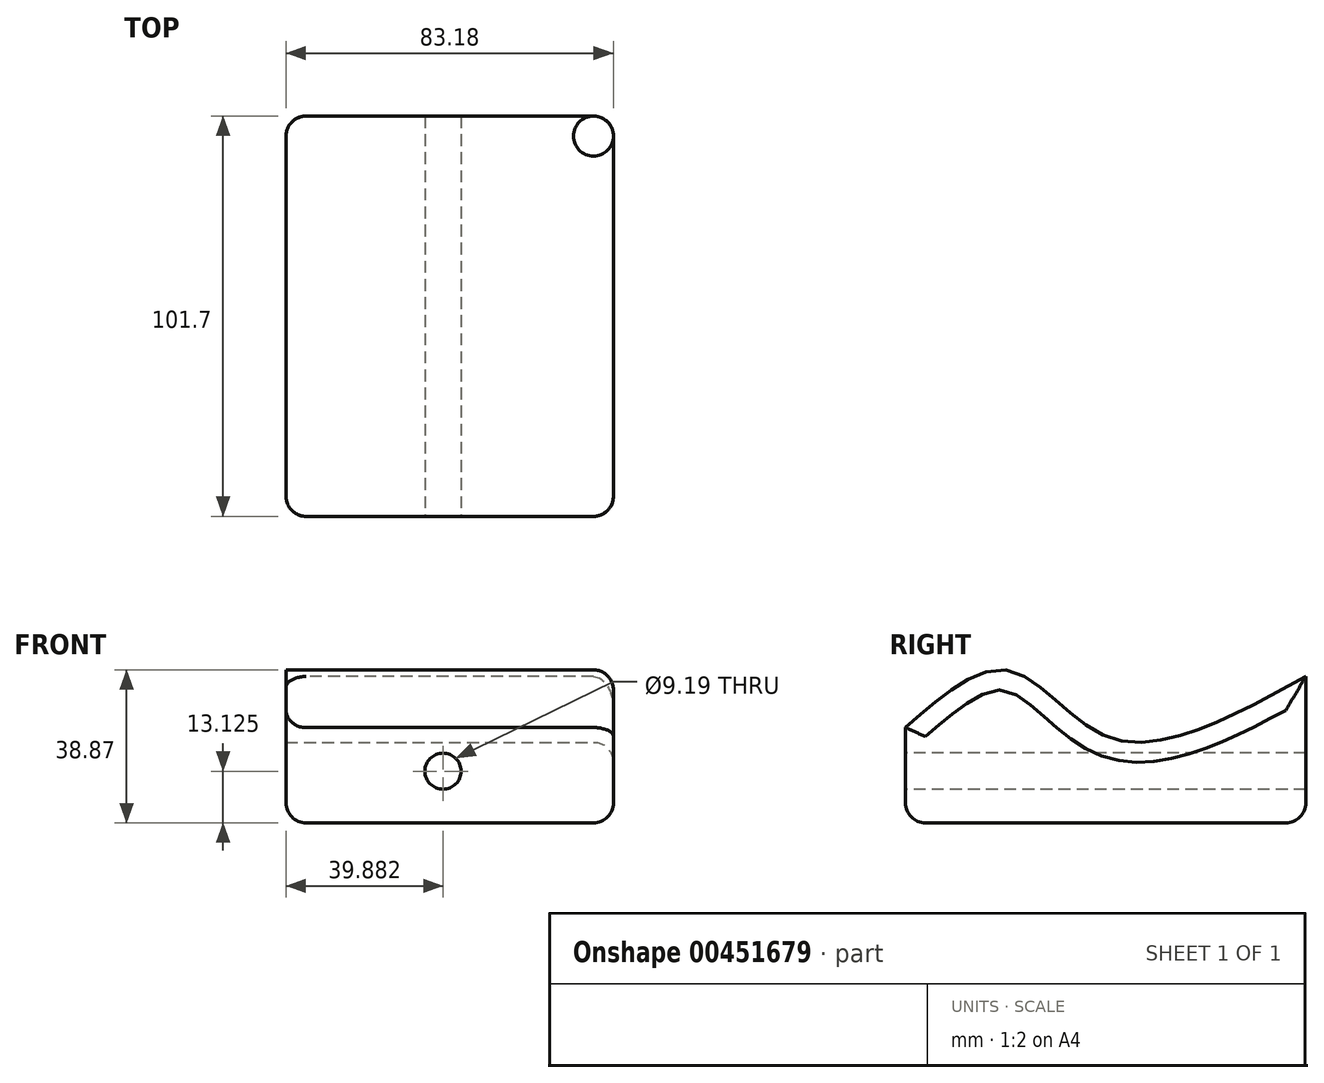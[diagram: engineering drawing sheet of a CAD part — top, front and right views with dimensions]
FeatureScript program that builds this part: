
annotation { "Feature Type Name" : "Feature", "Feature Type Description" : "" }
export const myFeature = defineFeature(function(context is Context, id is Id, definition is map)
    precondition{}
    {
        {
            var Q0;
            Q0=qCreatedBy(makeId("Top.planeOp"),FACE);
            var sketch = newSketch(context, id + "F0", { "sketchPlane" : qUnion([Q0])});
            skLineSegment(sketch, "E0.bottom", {"start": v(38.7, 44.88) * mm, "end": v(-44.47, 44.88) * mm});
            skLineSegment(sketch, "E0.top", {"start": v(38.7, -56.82) * mm, "end": v(-44.47, -56.82) * mm});
            skLineSegment(sketch, "E0.left", {"start": v(38.7, 44.88) * mm, "end": v(38.7, -56.82) * mm});
            skLineSegment(sketch, "E0.right", {"start": v(-44.47, 44.88) * mm, "end": v(-44.47, -56.82) * mm});
            skSolve(sketch);
        }
        {
            var Q0;
            Q0 = qSketchRegion(id + "F0", true);
            extrude(context, id + "F1", {"entities" : qUnion([Q0]), "depth" : 56.64 * mm});
        }
        {
            var Q0;
            Q0=makeQuery(id+"F1.opExtrude","SWEPT_FACE",FACE,{"disambiguationData":[OSD([sQuery(id+"F0.wireOp",EDGE,"E0.right")])]});
            var sketch = newSketch(context, id + "F2", { "sketchPlane" : qUnion([Q0])});
            skFitSpline(sketch, "E1", {"points": [v(-44.88, 37.17) * mm, v(4.53, 21.53) * mm, v(30.26, 38.61) * mm, v(56.82, 24.2) * mm], "startDerivative": vector(137.73, -76.07) * mm, "endDerivative": vector(91.5, -80.7) * mm});
            skLineSegment(sketch, "E2", {"start": v(-44.88, 37.17) * mm, "end": v(-44.88, 56.64) * mm});
            skLineSegment(sketch, "E3", {"start": v(-44.88, 56.64) * mm, "end": v(56.82, 56.64) * mm});
            skLineSegment(sketch, "E4", {"start": v(56.82, 56.64) * mm, "end": v(56.82, 24.2) * mm});
            skSolve(sketch);
        }
        {
            var Q0;
            Q0=makeQuery(id+"F2.imprint","IMPRINT",FACE,{"disambiguationData":[TD([[makeQuery(id+"F2.imprint","IMPRINT",EDGE,{"derivedFrom":sQuery(id+"F2.wireOp",EDGE,"E1")}),1.0]])]});
            extrude(context, id + "F3", {"entities" : qUnion([Q0]), "operationType" : NewBodyOperationType.REMOVE, "oppositeDirection" : true, "depth" : 112.01 * mm});
        }
        {
            var Q0;
            Q0=makeQuery(id+"F1.opExtrude","SWEPT_EDGE",EDGE,{"disambiguationData":[OSD([sQuery(id+"F0.wireOp",EDGE,"E0.top"),sQuery(id+"F0.wireOp",EDGE,"E0.right")])]});
            var Q1;
            Q1=makeQuery(id+"F1.opExtrude","SWEPT_EDGE",EDGE,{"disambiguationData":[OSD([sQuery(id+"F0.wireOp",EDGE,"E0.top"),sQuery(id+"F0.wireOp",EDGE,"E0.left")])]});
            var Q2;
            Q2=makeQuery(id+"F1.opExtrude","SWEPT_EDGE",EDGE,{"disambiguationData":[OSD([sQuery(id+"F0.wireOp",EDGE,"E0.bottom"),sQuery(id+"F0.wireOp",EDGE,"E0.right")])]});
            var Q3;
            Q3=makeQuery(id+"F1.opExtrude","SWEPT_EDGE",EDGE,{"disambiguationData":[OSD([sQuery(id+"F0.wireOp",EDGE,"E0.bottom"),sQuery(id+"F0.wireOp",EDGE,"E0.left")])]});
            var Q4;
            Q4=makeQuery(id+"F3.boolean.opBoolean","COPY",EDGE,{"derivedFrom":makeQuery(id+"F3.opExtrude","SWEPT_EDGE",EDGE,{"disambiguationData":[OSD([sQuery(id+"F0.wireOp",EDGE,"E0.bottom"),sQuery(id+"F0.wireOp",EDGE,"E0.right"),sQuery(id+"F2.wireOp",EDGE,"E1"),sQuery(id+"F2.wireOp",EDGE,"E2")])]})});
            var Q5;
            Q5=makeQuery(id+"F1.opExtrude","CAP_EDGE",EDGE,{"disambiguationData":[OSD([sQuery(id+"F0.wireOp",EDGE,"E0.bottom")])],"isStart":true});
            var Q6;
            Q6=makeQuery(id+"F3.boolean.opBoolean","INTERSECT",EDGE,{"derivedFrom":[makeQuery(id+"F1.opExtrude","SWEPT_FACE",FACE,{"disambiguationData":[OSD([sQuery(id+"F0.wireOp",EDGE,"E0.left")])]}),makeQuery(id+"F3.opExtrude","SWEPT_FACE",FACE,{"disambiguationData":[OSD([sQuery(id+"F2.wireOp",EDGE,"E1")])]})]});
            var Q7;
            Q7=makeQuery(id+"F1.opExtrude","CAP_EDGE",EDGE,{"disambiguationData":[OSD([sQuery(id+"F0.wireOp",EDGE,"E0.left")])],"isStart":true});
            var Q8;
            Q8=makeQuery(id+"F3.boolean.opBoolean","COPY",EDGE,{"derivedFrom":makeQuery(id+"F3.opExtrude","CAP_EDGE",EDGE,{"disambiguationData":[OSD([sQuery(id+"F2.wireOp",EDGE,"E1")])],"isStart":true})});
            var Q9;
            Q9=makeQuery(id+"F1.opExtrude","CAP_EDGE",EDGE,{"disambiguationData":[OSD([sQuery(id+"F0.wireOp",EDGE,"E0.right")])],"isStart":true});
            var Q10;
            Q10=makeQuery(id+"F1.opExtrude","CAP_EDGE",EDGE,{"disambiguationData":[OSD([sQuery(id+"F0.wireOp",EDGE,"E0.top")])],"isStart":true});
            var Q11;
            Q11=makeQuery(id+"F3.boolean.opBoolean","COPY",EDGE,{"derivedFrom":makeQuery(id+"F3.opExtrude","SWEPT_EDGE",EDGE,{"disambiguationData":[OSD([sQuery(id+"F0.wireOp",EDGE,"E0.top"),sQuery(id+"F0.wireOp",EDGE,"E0.right"),sQuery(id+"F2.wireOp",EDGE,"E1"),sQuery(id+"F2.wireOp",EDGE,"E4")])]})});
            fillet(context, id + "F4", {"entities" : qUnion([Q0, Q1, Q2, Q3, Q4, Q5, Q6, Q7, Q8, Q9, Q10, Q11]), "radius" : 5.08 * mm, "tangentPropagation" : true, "allowEdgeOverflow" : false});
        }
        {
            var Q0;
            Q0=makeQuery(id+"F1.opExtrude","SWEPT_FACE",FACE,{"disambiguationData":[OSD([sQuery(id+"F0.wireOp",EDGE,"E0.top")])]});
            var sketch = newSketch(context, id + "F5", { "sketchPlane" : qUnion([Q0])});
            skCircle(sketch, "E5", {"center": v(-4.59, 13.12) * mm, "radius": 4.6 * mm});
            skSolve(sketch);
        }
        {
            var Q0;
            Q0=makeQuery(id+"F5.imprint","IMPRINT",FACE,{"disambiguationData":[TD([[makeQuery(id+"F5.imprint","IMPRINT",EDGE,{"derivedFrom":sQuery(id+"F5.wireOp",EDGE,"E5")}),1.0]])]});
            extrude(context, id + "F6", {"entities" : qUnion([Q0]), "operationType" : NewBodyOperationType.REMOVE, "oppositeDirection" : true, "depth" : 141.73 * mm});
        }
    });
